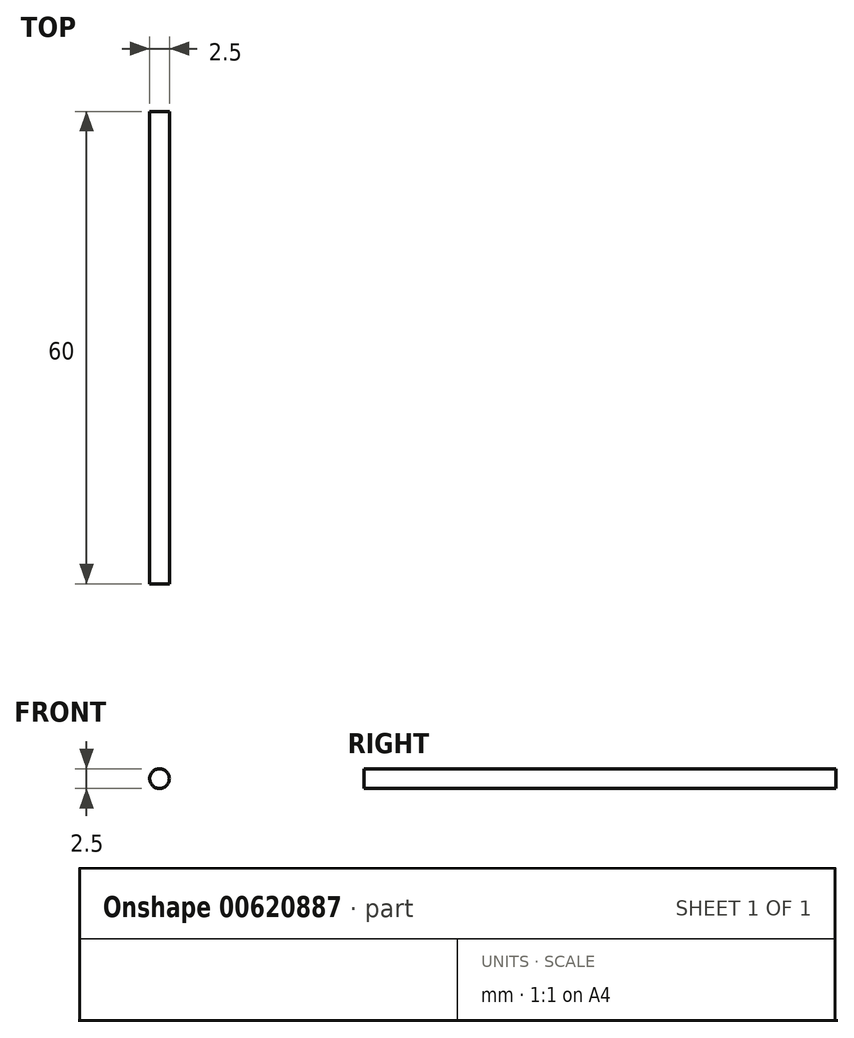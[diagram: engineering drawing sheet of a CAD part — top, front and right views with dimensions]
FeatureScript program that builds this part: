
annotation { "Feature Type Name" : "Feature", "Feature Type Description" : "" }
export const myFeature = defineFeature(function(context is Context, id is Id, definition is map)
    precondition{}
    {
        {
            var Q0;
            Q0=qCreatedBy(makeId("Front.planeOp"),FACE);
            var sketch = newSketch(context, id + "F0", { "sketchPlane" : qUnion([Q0])});
            skCircle(sketch, "E0", {"center": v(0, 0) * mm, "radius": 1.25 * mm});
            skSolve(sketch);
        }
        {
            var Q0;
            Q0=makeQuery(id+"F0.imprint","IMPRINT",FACE,{"disambiguationData":[TD([[makeQuery(id+"F0.imprint","IMPRINT",EDGE,{"derivedFrom":sQuery(id+"F0.wireOp",EDGE,"E0")}),1.0]])]});
            extrude(context, id + "F1", {"entities" : qUnion([Q0]), "depth" : 60 * mm, "offsetDistance" : 25 * mm});
        }
    });
